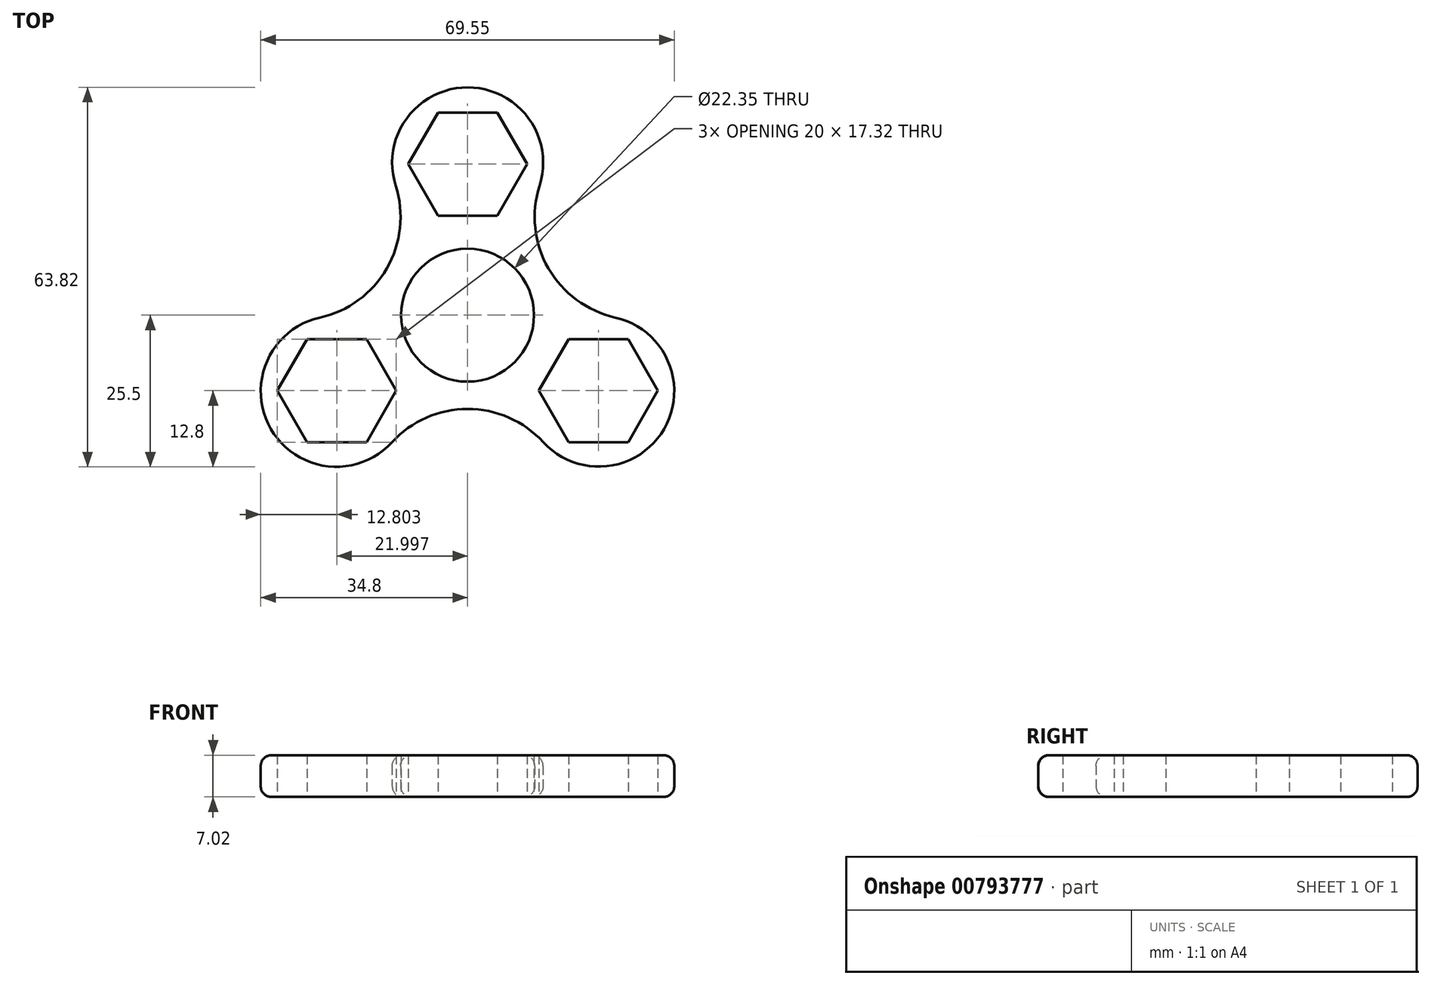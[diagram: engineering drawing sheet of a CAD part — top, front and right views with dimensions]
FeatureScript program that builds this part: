
annotation { "Feature Type Name" : "Feature", "Feature Type Description" : "" }
export const myFeature = defineFeature(function(context is Context, id is Id, definition is map)
    precondition{}
    {
        {
            var Q0;
            Q0=qCreatedBy(makeId("Top.planeOp"),FACE);
            var sketch = newSketch(context, id + "F0", { "sketchPlane" : qUnion([Q0])});
            skCircle(sketch, "E0", {"center": v(0, 0) * mm, "radius": 11.18 * mm});
            skCircle(sketch, "E1.cCircle", {"center": v(0, 25.4) * mm, "radius": 8.66 * mm, "construction": true});
            skLineSegment(sketch, "E1.0", {"start": v(5, 16.74) * mm, "end": v(-5, 16.74) * mm});
            skLineSegment(sketch, "E1.1", {"start": v(-5, 16.74) * mm, "end": v(-10, 25.4) * mm});
            skLineSegment(sketch, "E1.2", {"start": v(-10, 25.4) * mm, "end": v(-5, 34.06) * mm});
            skLineSegment(sketch, "E1.3", {"start": v(-5, 34.06) * mm, "end": v(5, 34.06) * mm});
            skLineSegment(sketch, "E1.4", {"start": v(5, 34.06) * mm, "end": v(10, 25.4) * mm});
            skLineSegment(sketch, "E1.5", {"start": v(10, 25.4) * mm, "end": v(5, 16.74) * mm});
            skPoint(sketch, "E1.0.midPoint", {"position": v(0, 16.74) * mm});
            skCircle(sketch, "E2.cCircle", {"center": v(22, -12.7) * mm, "radius": 8.66 * mm, "construction": true});
            skLineSegment(sketch, "E2.0", {"start": v(12, -12.7) * mm, "end": v(17, -4.04) * mm});
            skLineSegment(sketch, "E2.1", {"start": v(17, -4.04) * mm, "end": v(27, -4.04) * mm});
            skLineSegment(sketch, "E2.2", {"start": v(27, -4.04) * mm, "end": v(32, -12.7) * mm});
            skLineSegment(sketch, "E2.3", {"start": v(32, -12.7) * mm, "end": v(27, -21.36) * mm});
            skLineSegment(sketch, "E2.4", {"start": v(27, -21.36) * mm, "end": v(17, -21.36) * mm});
            skLineSegment(sketch, "E2.5", {"start": v(17, -21.36) * mm, "end": v(12, -12.7) * mm});
            skPoint(sketch, "E2.0.midPoint", {"position": v(14.5, -8.37) * mm});
            skCircle(sketch, "E3.cCircle", {"center": v(-22, -12.7) * mm, "radius": 8.66 * mm, "construction": true});
            skLineSegment(sketch, "E3.0", {"start": v(-17, -4.04) * mm, "end": v(-12, -12.7) * mm});
            skLineSegment(sketch, "E3.1", {"start": v(-12, -12.7) * mm, "end": v(-17, -21.36) * mm});
            skLineSegment(sketch, "E3.2", {"start": v(-17, -21.36) * mm, "end": v(-27, -21.36) * mm});
            skLineSegment(sketch, "E3.3", {"start": v(-27, -21.36) * mm, "end": v(-32, -12.7) * mm});
            skLineSegment(sketch, "E3.4", {"start": v(-32, -12.7) * mm, "end": v(-27, -4.04) * mm});
            skLineSegment(sketch, "E3.5", {"start": v(-27, -4.04) * mm, "end": v(-17, -4.04) * mm});
            skPoint(sketch, "E3.0.midPoint", {"position": v(-14.5, -8.37) * mm});
            skArc(sketch, "E4", {"start": v(-12.73, -21.37) * mm, "mid": v(-0.01, -15.76) * mm, "end": v(12.72, -21.35) * mm});
            skArc(sketch, "E5", {"start": v(-24.85, -0.4) * mm, "mid": v(-13.59, 7.87) * mm, "end": v(-12.1, 21.77) * mm});
            skArc(sketch, "E6", {"start": v(12.1, 21.76) * mm, "mid": v(13.59, 7.89) * mm, "end": v(24.83, -0.39) * mm});
            skArc(sketch, "E7", {"start": v(-24.85, -0.4) * mm, "mid": v(-33.1, -19.15) * mm, "end": v(-12.73, -21.37) * mm});
            skArc(sketch, "E8", {"start": v(12.1, 21.76) * mm, "mid": v(0, 38.32) * mm, "end": v(-12.1, 21.77) * mm});
            skArc(sketch, "E9", {"start": v(12.72, -21.35) * mm, "mid": v(33.05, -19.12) * mm, "end": v(24.83, -0.39) * mm});
            skSolve(sketch);
        }
        {
            var Q0;
            Q0=makeQuery(id+"F0.imprint","IMPRINT",FACE,{"disambiguationData":[TD([[makeQuery(id+"F0.imprint","IMPRINT",EDGE,{"derivedFrom":sQuery(id+"F0.wireOp",EDGE,"E3.0")}),1.0]])]});
            var Q1;
            Q1=makeQuery(id+"F0.imprint","IMPRINT",FACE,{"disambiguationData":[TD([[makeQuery(id+"F0.imprint","IMPRINT",EDGE,{"derivedFrom":sQuery(id+"F0.wireOp",EDGE,"E2.0")}),1.0]])]});
            var Q2;
            Q2=makeQuery(id+"F0.imprint","IMPRINT",FACE,{"disambiguationData":[TD([[makeQuery(id+"F0.imprint","IMPRINT",EDGE,{"derivedFrom":sQuery(id+"F0.wireOp",EDGE,"E0")}),-1.0]])]});
            var Q3;
            Q3=makeQuery(id+"F0.imprint","IMPRINT",FACE,{"disambiguationData":[TD([[makeQuery(id+"F0.imprint","IMPRINT",EDGE,{"derivedFrom":sQuery(id+"F0.wireOp",EDGE,"E1.0")}),1.0]])]});
            extrude(context, id + "F1", {"entities" : qUnion([Q0, Q1, Q2, Q3]), "endBound" : BoundingType.SYMMETRIC, "depth" : 7 * mm, "offsetDistance" : 25.4 * mm});
        }
        {
            var Q0;
            Q0=makeQuery(id+"F1.opExtrude","CAP_EDGE",EDGE,{"disambiguationData":[OSD([sQuery(id+"F0.wireOp",EDGE,"E7")])],"isStart":false});
            var Q1;
            Q1=makeQuery(id+"F1.opExtrude","CAP_EDGE",EDGE,{"disambiguationData":[OSD([sQuery(id+"F0.wireOp",EDGE,"E4")])],"isStart":false});
            var Q2;
            Q2=makeQuery(id+"F1.opExtrude","CAP_EDGE",EDGE,{"disambiguationData":[OSD([sQuery(id+"F0.wireOp",EDGE,"E5")])],"isStart":false});
            var Q3;
            Q3=makeQuery(id+"F1.opExtrude","CAP_EDGE",EDGE,{"disambiguationData":[OSD([sQuery(id+"F0.wireOp",EDGE,"E8")])],"isStart":false});
            var Q4;
            Q4=makeQuery(id+"F1.opExtrude","CAP_EDGE",EDGE,{"disambiguationData":[OSD([sQuery(id+"F0.wireOp",EDGE,"E6")])],"isStart":false});
            var Q5;
            Q5=makeQuery(id+"F1.opExtrude","CAP_EDGE",EDGE,{"disambiguationData":[OSD([sQuery(id+"F0.wireOp",EDGE,"E9")])],"isStart":false});
            var Q6;
            Q6=makeQuery(id+"F1.opExtrude","CAP_EDGE",EDGE,{"disambiguationData":[OSD([sQuery(id+"F0.wireOp",EDGE,"E6")])],"isStart":true});
            var Q7;
            Q7=makeQuery(id+"F1.opExtrude","CAP_EDGE",EDGE,{"disambiguationData":[OSD([sQuery(id+"F0.wireOp",EDGE,"E8")])],"isStart":true});
            var Q8;
            Q8=makeQuery(id+"F1.opExtrude","CAP_EDGE",EDGE,{"disambiguationData":[OSD([sQuery(id+"F0.wireOp",EDGE,"E5")])],"isStart":true});
            var Q9;
            Q9=makeQuery(id+"F1.opExtrude","CAP_EDGE",EDGE,{"disambiguationData":[OSD([sQuery(id+"F0.wireOp",EDGE,"E7")])],"isStart":true});
            var Q10;
            Q10=makeQuery(id+"F1.opExtrude","CAP_EDGE",EDGE,{"disambiguationData":[OSD([sQuery(id+"F0.wireOp",EDGE,"E4")])],"isStart":true});
            var Q11;
            Q11=makeQuery(id+"F1.opExtrude","CAP_EDGE",EDGE,{"disambiguationData":[OSD([sQuery(id+"F0.wireOp",EDGE,"E9")])],"isStart":true});
            fillet(context, id + "F2", {"entities" : qUnion([Q0, Q1, Q2, Q3, Q4, Q5, Q6, Q7, Q8, Q9, Q10, Q11]), "radius" : 1.78 * mm, "tangentPropagation" : true, "allowEdgeOverflow" : false});
        }
    });
